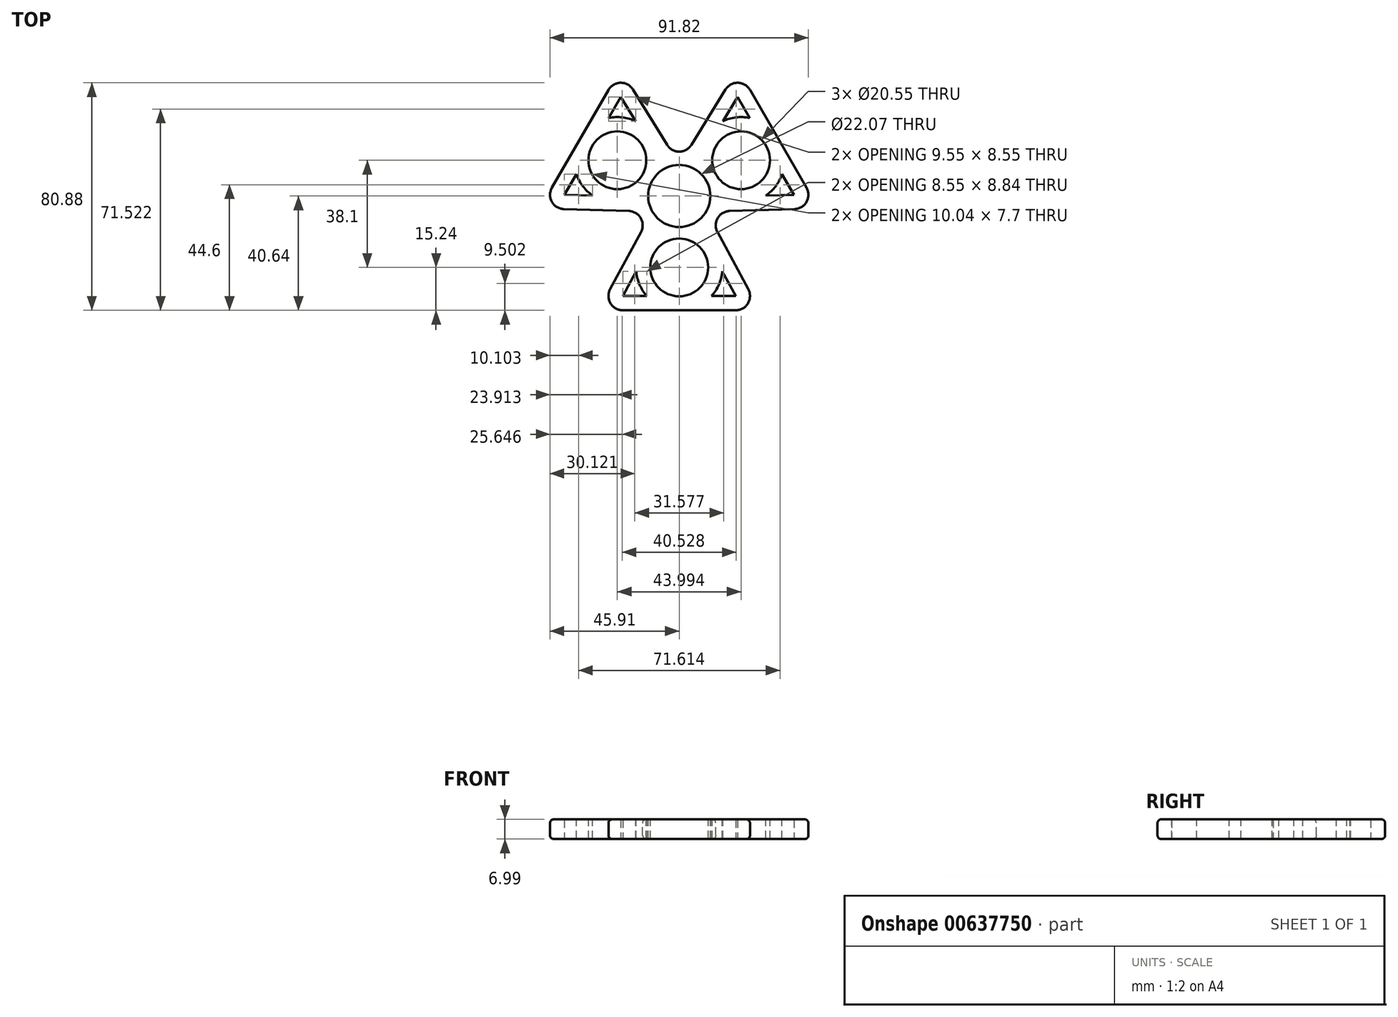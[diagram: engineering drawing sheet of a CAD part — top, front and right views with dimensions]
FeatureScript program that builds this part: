
annotation { "Feature Type Name" : "Feature", "Feature Type Description" : "" }
export const myFeature = defineFeature(function(context is Context, id is Id, definition is map)
    precondition{}
    {
        {
            var Q0;
            Q0=qCreatedBy(makeId("Top.planeOp"),FACE);
            var sketch = newSketch(context, id + "F0", { "sketchPlane" : qUnion([Q0])});
            skCircle(sketch, "E0", {"center": v(0, 0) * mm, "radius": 11.04 * mm});
            skLineSegment(sketch, "E1", {"start": v(0, 0) * mm, "end": v(22, 12.7) * mm});
            skLineSegment(sketch, "E2", {"start": v(0, 0) * mm, "end": v(0, -25.4) * mm});
            skLineSegment(sketch, "E3", {"start": v(0, 0) * mm, "end": v(-22, 12.7) * mm});
            skCircle(sketch, "E4", {"center": v(-22, 12.7) * mm, "radius": 10.27 * mm});
            skCircle(sketch, "E5", {"center": v(22, 12.7) * mm, "radius": 10.27 * mm});
            skCircle(sketch, "E6", {"center": v(0, -25.4) * mm, "radius": 10.27 * mm});
            skLineSegment(sketch, "E7", {"start": v(-49.48, -4.43) * mm, "end": v(-20.9, 45.07) * mm});
            skLineSegment(sketch, "E8", {"start": v(-20.9, 45.07) * mm, "end": v(0, 11.18) * mm});
            skLineSegment(sketch, "E9", {"start": v(-49.48, -4.43) * mm, "end": v(-9.68, -5.59) * mm});
            skLineSegment(sketch, "E10", {"start": v(0, 0) * mm, "end": v(-49.09, -28.34) * mm});
            skLineSegment(sketch, "E11", {"start": v(0, 0) * mm, "end": v(0, 59.9) * mm});
            skLineSegment(sketch, "E12", {"start": v(0, 0) * mm, "end": v(54.39, -31.4) * mm});
            skLineSegment(sketch, "E13", {"start": v(-22, 12.7) * mm, "end": v(-35.2, 20.32) * mm});
            skLineSegment(sketch, "E14.1.0", {"start": v(28.58, -40.64) * mm, "end": v(9.68, -5.59) * mm});
            skLineSegment(sketch, "E14.1.1", {"start": v(28.58, -40.64) * mm, "end": v(-28.57, -40.64) * mm});
            skLineSegment(sketch, "E14.1.2", {"start": v(0, -25.4) * mm, "end": v(0, -40.64) * mm});
            skLineSegment(sketch, "E14.1.3", {"start": v(-28.57, -40.64) * mm, "end": v(-9.68, -5.59) * mm});
            skLineSegment(sketch, "E14.2.0", {"start": v(20.9, 45.07) * mm, "end": v(0, 11.18) * mm});
            skLineSegment(sketch, "E14.2.1", {"start": v(20.9, 45.07) * mm, "end": v(49.48, -4.43) * mm});
            skLineSegment(sketch, "E14.2.2", {"start": v(22, 12.7) * mm, "end": v(35.2, 20.32) * mm});
            skLineSegment(sketch, "E14.2.3", {"start": v(49.48, -4.43) * mm, "end": v(9.68, -5.59) * mm});
            skCircle(sketch, "E15", {"center": v(0, 0) * mm, "radius": 15.13 * mm});
            skSolve(sketch);
        }
        {
            var Q0;
            {var subQ0=sQuery(id+"F0.wireOp",EDGE,"E14.2.0");Q0=makeQuery(id+"F0.imprint","IMPRINT",FACE,{"disambiguationData":[TD([[makeQuery(id+"F0.imprint","IMPRINT",EDGE,{"derivedFrom":subQ0}),1.0]])]});}
            var Q1;
            {var subQ0=sQuery(id+"F0.wireOp",EDGE,"E8");Q1=makeQuery(id+"F0.imprint","IMPRINT",FACE,{"disambiguationData":[TD([[makeQuery(id+"F0.imprint","IMPRINT",EDGE,{"derivedFrom":subQ0}),-1.0]])]});}
            var Q2;
            {var subQ0=sQuery(id+"F0.wireOp",EDGE,"E9");Q2=makeQuery(id+"F0.imprint","IMPRINT",FACE,{"disambiguationData":[TD([[makeQuery(id+"F0.imprint","IMPRINT",EDGE,{"derivedFrom":subQ0}),1.0]])]});}
            var Q3;
            {var subQ0=sQuery(id+"F0.wireOp",EDGE,"E14.1.3");Q3=makeQuery(id+"F0.imprint","IMPRINT",FACE,{"disambiguationData":[TD([[makeQuery(id+"F0.imprint","IMPRINT",EDGE,{"derivedFrom":subQ0}),-1.0]])]});}
            var Q4;
            {var subQ0=sQuery(id+"F0.wireOp",EDGE,"E14.1.0");Q4=makeQuery(id+"F0.imprint","IMPRINT",FACE,{"disambiguationData":[TD([[makeQuery(id+"F0.imprint","IMPRINT",EDGE,{"derivedFrom":subQ0}),1.0]])]});}
            var Q5;
            {var subQ0=sQuery(id+"F0.wireOp",EDGE,"E14.2.3");Q5=makeQuery(id+"F0.imprint","IMPRINT",FACE,{"disambiguationData":[TD([[makeQuery(id+"F0.imprint","IMPRINT",EDGE,{"derivedFrom":subQ0}),-1.0]])]});}
            extrude(context, id + "F1", {"entities" : qUnion([Q0, Q1, Q2, Q3, Q4, Q5]), "oppositeDirection" : true, "depth" : 7 * mm, "offsetDistance" : 25.4 * mm});
        }
        {
            var Q0;
            Q0=makeQuery(id+"F1.opExtrude","SWEPT_EDGE",EDGE,{"disambiguationData":[OSD([sQuery(id+"F0.wireOp",EDGE,"E7"),sQuery(id+"F0.wireOp",EDGE,"E8")])]});
            var Q1;
            Q1=makeQuery(id+"F1.opExtrude","SWEPT_EDGE",EDGE,{"disambiguationData":[OSD([sQuery(id+"F0.wireOp",EDGE,"E14.2.0"),sQuery(id+"F0.wireOp",EDGE,"E14.2.1")])]});
            var Q2;
            Q2=makeQuery(id+"F1.opExtrude","SWEPT_EDGE",EDGE,{"disambiguationData":[OSD([sQuery(id+"F0.wireOp",EDGE,"E14.2.1"),sQuery(id+"F0.wireOp",EDGE,"E14.2.3")])]});
            var Q3;
            Q3=makeQuery(id+"F1.opExtrude","SWEPT_EDGE",EDGE,{"disambiguationData":[OSD([sQuery(id+"F0.wireOp",EDGE,"E14.1.0"),sQuery(id+"F0.wireOp",EDGE,"E14.1.1")])]});
            var Q4;
            Q4=makeQuery(id+"F1.opExtrude","SWEPT_EDGE",EDGE,{"disambiguationData":[OSD([sQuery(id+"F0.wireOp",EDGE,"E14.1.1"),sQuery(id+"F0.wireOp",EDGE,"E14.1.3")])]});
            var Q5;
            Q5=makeQuery(id+"F1.opExtrude","SWEPT_EDGE",EDGE,{"disambiguationData":[OSD([sQuery(id+"F0.wireOp",EDGE,"E7"),sQuery(id+"F0.wireOp",EDGE,"E9")])]});
            fillet(context, id + "F2", {"entities" : qUnion([Q0, Q1, Q2, Q3, Q4, Q5]), "radius" : 5.08 * mm, "tangentPropagation" : true, "allowEdgeOverflow" : false});
        }
        {
            var Q0;
            Q0=makeQuery(id+"F1.opExtrude","SWEPT_EDGE",EDGE,{"disambiguationData":[OSD([sQuery(id+"F0.wireOp",EDGE,"E8"),sQuery(id+"F0.wireOp",EDGE,"E11"),sQuery(id+"F0.wireOp",EDGE,"E14.2.0")])]});
            var Q1;
            Q1=makeQuery(id+"F1.opExtrude","SWEPT_EDGE",EDGE,{"disambiguationData":[OSD([sQuery(id+"F0.wireOp",EDGE,"E12"),sQuery(id+"F0.wireOp",EDGE,"E14.1.0"),sQuery(id+"F0.wireOp",EDGE,"E14.2.3")])]});
            var Q2;
            Q2=makeQuery(id+"F1.opExtrude","SWEPT_EDGE",EDGE,{"disambiguationData":[OSD([sQuery(id+"F0.wireOp",EDGE,"E9"),sQuery(id+"F0.wireOp",EDGE,"E10"),sQuery(id+"F0.wireOp",EDGE,"E14.1.3")])]});
            fillet(context, id + "F3", {"entities" : qUnion([Q0, Q1, Q2]), "radius" : 5.08 * mm, "tangentPropagation" : true, "allowEdgeOverflow" : false});
        }
        {
            var Q0;
            Q0=makeQuery(id+"F1.opExtrude","CAP_EDGE",EDGE,{"disambiguationData":[OSD([sQuery(id+"F0.wireOp",EDGE,"E7")])],"isStart":true});
            fillet(context, id + "F4", {"entities" : qUnion([Q0]), "radius" : 1.27 * mm, "tangentPropagation" : true, "allowEdgeOverflow" : false});
        }
        {
            var Q0;
            Q0=makeQuery(id+"F1.opExtrude","CAP_EDGE",EDGE,{"disambiguationData":[OSD([sQuery(id+"F0.wireOp",EDGE,"E14.2.1")])],"isStart":false});
            fillet(context, id + "F5", {"entities" : qUnion([Q0]), "radius" : 1.27 * mm, "tangentPropagation" : true, "allowEdgeOverflow" : false});
        }
        {
            var Q0;
            Q0=makeQuery(id+"F1.opExtrude","CAP_FACE",FACE,{"disambiguationData":[OSD([sQuery(id+"F0.wireOp",EDGE,"E0"),sQuery(id+"F0.wireOp",EDGE,"E4"),sQuery(id+"F0.wireOp",EDGE,"E5"),sQuery(id+"F0.wireOp",EDGE,"E6"),sQuery(id+"F0.wireOp",EDGE,"E7"),sQuery(id+"F0.wireOp",EDGE,"E8"),sQuery(id+"F0.wireOp",EDGE,"E9"),sQuery(id+"F0.wireOp",EDGE,"E14.1.0"),sQuery(id+"F0.wireOp",EDGE,"E14.1.1"),sQuery(id+"F0.wireOp",EDGE,"E14.1.3"),sQuery(id+"F0.wireOp",EDGE,"E14.2.0"),sQuery(id+"F0.wireOp",EDGE,"E14.2.1"),sQuery(id+"F0.wireOp",EDGE,"E14.2.3")])],"isStart":false});
            var Q1;
            Q1=makeQuery(id+"F1.opExtrude","CAP_FACE",FACE,{"disambiguationData":[OSD([sQuery(id+"F0.wireOp",EDGE,"E0"),sQuery(id+"F0.wireOp",EDGE,"E4"),sQuery(id+"F0.wireOp",EDGE,"E5"),sQuery(id+"F0.wireOp",EDGE,"E6"),sQuery(id+"F0.wireOp",EDGE,"E7"),sQuery(id+"F0.wireOp",EDGE,"E8"),sQuery(id+"F0.wireOp",EDGE,"E9"),sQuery(id+"F0.wireOp",EDGE,"E14.1.0"),sQuery(id+"F0.wireOp",EDGE,"E14.1.1"),sQuery(id+"F0.wireOp",EDGE,"E14.1.3"),sQuery(id+"F0.wireOp",EDGE,"E14.2.0"),sQuery(id+"F0.wireOp",EDGE,"E14.2.1"),sQuery(id+"F0.wireOp",EDGE,"E14.2.3")])],"isStart":true});
            shell(context, id + "F6", {"entities" : qUnion([Q0, Q1]), "thickness" : 5.08 * mm});
        }
    });
